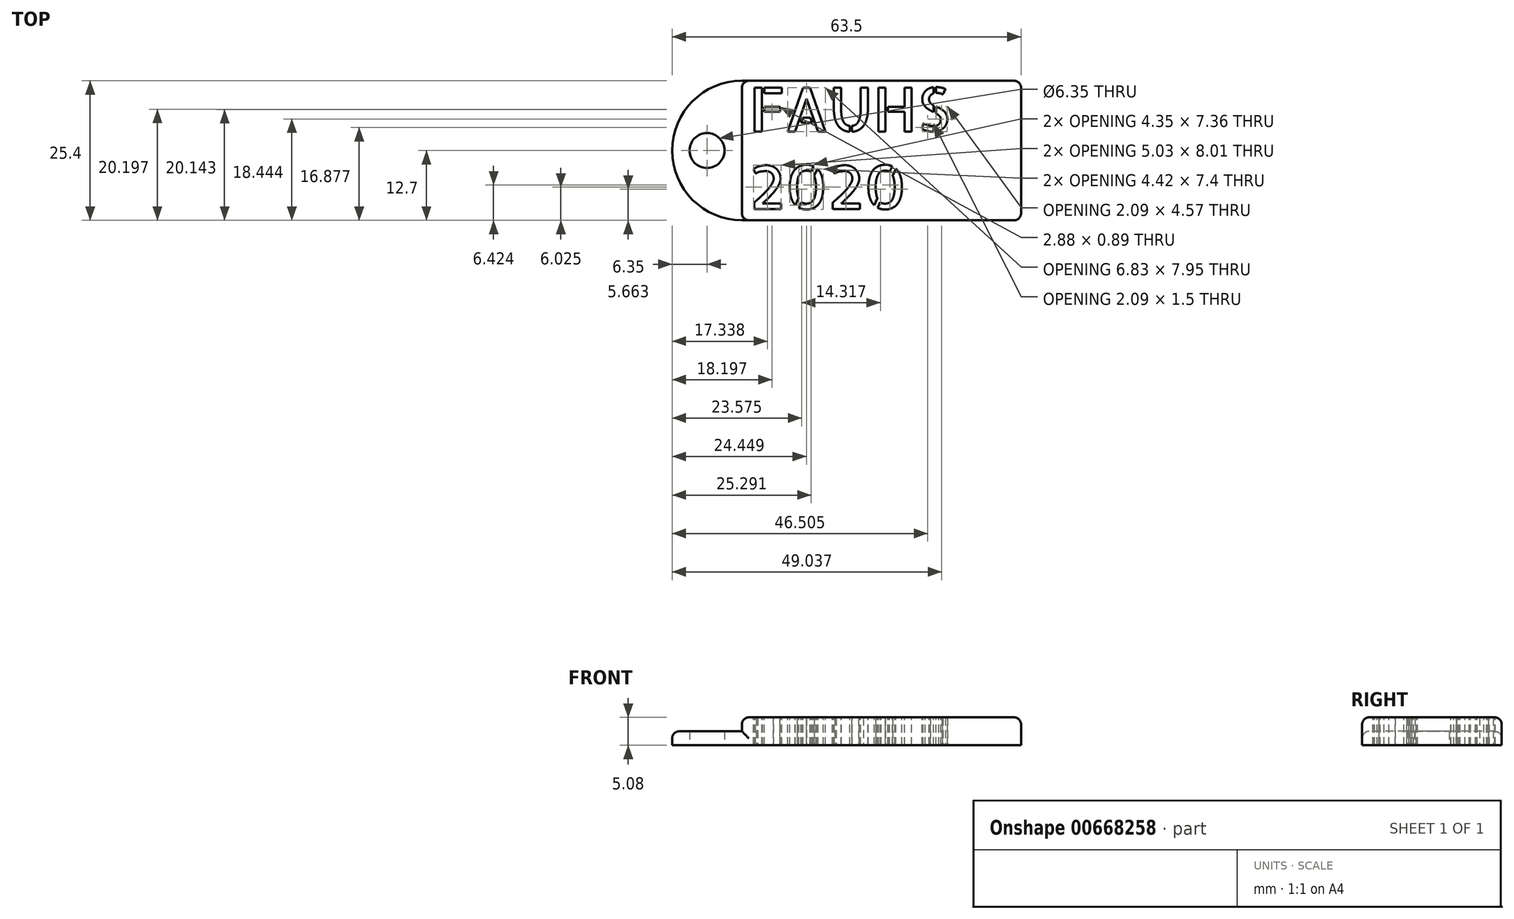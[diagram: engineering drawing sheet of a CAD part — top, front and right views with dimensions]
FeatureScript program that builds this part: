
annotation { "Feature Type Name" : "Feature", "Feature Type Description" : "" }
export const myFeature = defineFeature(function(context is Context, id is Id, definition is map)
    precondition{}
    {
        {
            var Q0;
            Q0=qCreatedBy(makeId("Top.planeOp"),FACE);
            var sketch = newSketch(context, id + "F0", { "sketchPlane" : qUnion([Q0])});
            skLineSegment(sketch, "E0.bottom", {"start": v(25.4, 12.7) * mm, "end": v(-25.4, 12.7) * mm});
            skLineSegment(sketch, "E0.top", {"start": v(25.4, -12.7) * mm, "end": v(-25.4, -12.7) * mm});
            skLineSegment(sketch, "E0.left", {"start": v(25.4, 12.7) * mm, "end": v(25.4, -12.7) * mm});
            skPoint(sketch, "E0.middle", {"position": v(0, 0) * mm});
            skArc(sketch, "E1", {"start": v(-25.4, 12.7) * mm, "mid": v(-38.1, 0) * mm, "end": v(-25.4, -12.7) * mm});
            skCircle(sketch, "E2", {"center": v(-31.75, 0) * mm, "radius": 3.18 * mm});
            skSolve(sketch);
        }
        {
            var Q0;
            Q0 = qSketchRegion(id + "F0", true);
            extrude(context, id + "F1", {"entities" : qUnion([Q0]), "depth" : 2.54 * mm, "offsetDistance" : 25.4 * mm});
        }
        {
            var Q0;
            Q0=makeQuery(id+"F1.opExtrude","CAP_FACE",FACE,{"disambiguationData":[OSD([sQuery(id+"F0.wireOp",EDGE,"E0.bottom"),sQuery(id+"F0.wireOp",EDGE,"E0.top"),sQuery(id+"F0.wireOp",EDGE,"E0.left"),sQuery(id+"F0.wireOp",EDGE,"E1"),sQuery(id+"F0.wireOp",EDGE,"E2")])],"isStart":false});
            var sketch = newSketch(context, id + "F2", { "sketchPlane" : qUnion([Q0])});
            skLineSegment(sketch, "E3.bottom", {"start": v(25.4, 12.7) * mm, "end": v(-25.4, 12.7) * mm});
            skLineSegment(sketch, "E3.top", {"start": v(25.4, -12.7) * mm, "end": v(-25.4, -12.7) * mm});
            skLineSegment(sketch, "E3.left", {"start": v(25.4, 12.7) * mm, "end": v(25.4, -12.7) * mm});
            skLineSegment(sketch, "E3.right", {"start": v(-25.4, 12.7) * mm, "end": v(-25.4, -12.7) * mm});
            skPoint(sketch, "E3.middle", {"position": v(0, 0) * mm});
            skSolve(sketch);
        }
        {
            var Q0;
            Q0 = qSketchRegion(id + "F2", true);
            extrude(context, id + "F3", {"entities" : qUnion([Q0]), "operationType" : NewBodyOperationType.ADD, "depth" : 2.54 * mm, "offsetDistance" : 25.4 * mm});
        }
        {
            var Q0;
            Q0=makeQuery(id+"F3.opExtrude","CAP_EDGE",EDGE,{"disambiguationData":[OSD([sQuery(id+"F2.wireOp",EDGE,"E3.bottom")])],"isStart":false});
            var Q1;
            Q1=makeQuery(id+"F3.opExtrude","CAP_EDGE",EDGE,{"disambiguationData":[OSD([sQuery(id+"F2.wireOp",EDGE,"E3.left")])],"isStart":false});
            var Q2;
            Q2=makeQuery(id+"F3.opExtrude","CAP_EDGE",EDGE,{"disambiguationData":[OSD([sQuery(id+"F2.wireOp",EDGE,"E3.top")])],"isStart":false});
            var Q3;
            Q3=makeQuery(id+"F3.opExtrude","CAP_EDGE",EDGE,{"disambiguationData":[OSD([sQuery(id+"F2.wireOp",EDGE,"E3.right")])],"isStart":false});
            var Q4;
            Q4=makeQuery(id+"F1.opExtrude","CAP_EDGE",EDGE,{"disambiguationData":[OSD([sQuery(id+"F0.wireOp",EDGE,"E1")])],"isStart":false});
            var Q5;
            Q5=makeQuery(id+"F3.opExtrude","CAP_EDGE",EDGE,{"disambiguationData":[OSD([sQuery(id+"F2.wireOp",EDGE,"E3.right")])],"isStart":true});
            var Q6;
            Q6=makeQuery(id+"F3.opExtrude","SWEPT_EDGE",EDGE,{"disambiguationData":[OSD([sQuery(id+"F0.wireOp",EDGE,"E1"),sQuery(id+"F2.wireOp",EDGE,"E3.bottom"),sQuery(id+"F2.wireOp",EDGE,"E3.right")])]});
            var Q7;
            Q7=makeQuery(id+"F3.opExtrude","SWEPT_EDGE",EDGE,{"disambiguationData":[OSD([sQuery(id+"F0.wireOp",EDGE,"E1"),sQuery(id+"F2.wireOp",EDGE,"E3.top"),sQuery(id+"F2.wireOp",EDGE,"E3.right")])]});
            var Q8;
            Q8=makeQuery(id+"F3.boolean.opBoolean","MERGE",EDGE,{"derivedFrom":[makeQuery(id+"F1.opExtrude","SWEPT_EDGE",EDGE,{"disambiguationData":[OSD([sQuery(id+"F0.wireOp",EDGE,"E0.bottom"),sQuery(id+"F0.wireOp",EDGE,"E0.left")])]}),makeQuery(id+"F3.opExtrude","SWEPT_EDGE",EDGE,{"disambiguationData":[OSD([sQuery(id+"F2.wireOp",EDGE,"E3.bottom"),sQuery(id+"F2.wireOp",EDGE,"E3.left")])]})]});
            var Q9;
            Q9=makeQuery(id+"F3.boolean.opBoolean","MERGE",EDGE,{"derivedFrom":[makeQuery(id+"F1.opExtrude","SWEPT_EDGE",EDGE,{"disambiguationData":[OSD([sQuery(id+"F0.wireOp",EDGE,"E0.top"),sQuery(id+"F0.wireOp",EDGE,"E0.left")])]}),makeQuery(id+"F3.opExtrude","SWEPT_EDGE",EDGE,{"disambiguationData":[OSD([sQuery(id+"F2.wireOp",EDGE,"E3.top"),sQuery(id+"F2.wireOp",EDGE,"E3.left")])]})]});
            fillet(context, id + "F4", {"entities" : qUnion([Q0, Q1, Q2, Q3, Q4, Q5, Q6, Q7, Q8, Q9]), "radius" : 1.27 * mm, "tangentPropagation" : true, "allowEdgeOverflow" : false});
        }
        {
            var Q0;
            Q0=makeQuery(id+"F3.opExtrude","CAP_FACE",FACE,{"disambiguationData":[OSD([sQuery(id+"F2.wireOp",EDGE,"E3.bottom"),sQuery(id+"F2.wireOp",EDGE,"E3.top"),sQuery(id+"F2.wireOp",EDGE,"E3.left"),sQuery(id+"F2.wireOp",EDGE,"E3.right")])],"isStart":false});
            var sketch = newSketch(context, id + "F5", { "sketchPlane" : qUnion([Q0])});
            skText(sketch, "E4", { "text": "FAUHS\n2020", "fontName": "AllertaStencil-Regular.ttf"});
            const initialGuessF5  = {"E4": [-0.02413, 0.00347, 1, 0, 0.00796]};
            skSetInitialGuess(sketch, initialGuessF5);
            skSolve(sketch);
        }
        {
            var Q0;
            Q0 = qSketchRegion(id + "F5", true);
            extrude(context, id + "F6", {"entities" : qUnion([Q0]), "operationType" : NewBodyOperationType.REMOVE, "oppositeDirection" : true, "depth" : 25.4 * mm, "offsetDistance" : 25.4 * mm});
        }
    });
